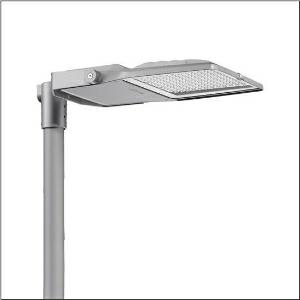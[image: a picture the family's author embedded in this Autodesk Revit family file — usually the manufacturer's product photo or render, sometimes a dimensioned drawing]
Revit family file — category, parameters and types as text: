
# Revit family: floodlight_fl_21_midi___pl61_5xa7786f2c3a_551f
name_source: partatom
category: Lighting Fixtures
units: mm (PartAtom-declared; Revit-internal decimal feet)

## family parameters
Cut with Voids When Loaded = No
Host = Face
Light Source = No
Part Type = Normal
Room Calculation Point = No
Round Connector Dimension = Use Diameter
Shared = No

## types (1)
- --- (1 x LED, 35100 lm, 271.6 W, 3000K)
    Apparent Load = 272 VA
    CIE Flux Codes = 33 65 98 100 100
    Color Rendering = 70
    Color Temperature = 3000K
    Default Elevation = 1800 mm
    Description = Floodlight FL 21 midi, floodlight, primary light control with lens, of PMMA, primary optical cover: protective disc, of toughened safety glass, transparent, light distribution: PL61, light emission: direct distribution, installation type: surface-mounted, LED, High Power LED, rated luminous flux: 35.100lm, luminous efficacy: 129lm/W, light colour: 730, colour temperature: 3000K, control gear: Smart Interface (Zhaga), control: flexible luminous flux parameterisation, time-dependent luminous flux control, constant luminous flux control, overheat protection, pre-setting: logarithmic dimming characteristic, with terminal, 6-pole, mains connection: 220..240V, AC, 50/60Hz, start of lifetime: 272W, end of service life: 287W, reduction: 123W, luminaire housing, of diecast aluminium, powder-coated, SITECO metallic grey (DB 702S), corrosivity category C5 mid according to DIN EN ISO 12944, suitable for swimming pools, chlorine-resistant, sealing non-destructively replaceable, please order mast flange separately, mast bracket, of steel, galvanised, powder-coated, SITECO metallic grey (DB 702S), Smart Interface below and above, protection rating (complete): IP66, insulation class (complete): insulation class II (safety insulation), certification: CE, ENEC, VDE, protection symbol: D, impact resistance: IK08, permissible operating ambient temperature: -40..+40°C, permissible operating ambient temperature for outdoor applications: -40..+50°C, standard: DIN EN 12944, LABS conformity tested according to VDMA 24364:2018-05, packaging unit: 1 piece

Light Distribution: PL61
    Height = 76 mm
    Lamp = 1 x LED
    Lamp Light Flux = 35100 lm
    Lamp Power = 271.6 W
    Lamp count = 1
    Length = 657 mm
    Luminous efficacy = 129 lm/W
    Manufacturer = Siteco
    ModVariant = No
    Model = 5XA7786F2C3A
    Number of Poles = 1
    OnlyDefault = Yes
    Power Factor = 1
    Product Name = Floodlight FL 21 midi | PL61
    Product group = floodlight | pylon annexe
    ProductGroupID = 6201
    Protection Class = Protection class II
    Protection Degree = IP 66
    RLX_Detail_Level = 1
    RLX_Emergency_Light_Flux = 0 lm
    RLX_Emergency_Type = 0
    RLX_Emergency_Type_DB = No
    RlxData = <blob elided: 153717 chars, md5=5f77f1b0>
    Socket = socket
    Standby Power = 0 W
    System Light Flux = 35100 lm
    System Power = 272 W
    Type Comments = factory setting: luminous flux: 100 % | dim-lin: 254 | 620 mA
    Type Image = l_1007123.jpg
    URL = http://relux.com
    VarID = @adj_191389
    Voltage = 0 V
    Weight = 0.00 kg
    Width = 442 mm

## geometry (parser evidence)
native form markers: Blend x4, Sweep x14
no freeform markers — native parametric forms only
